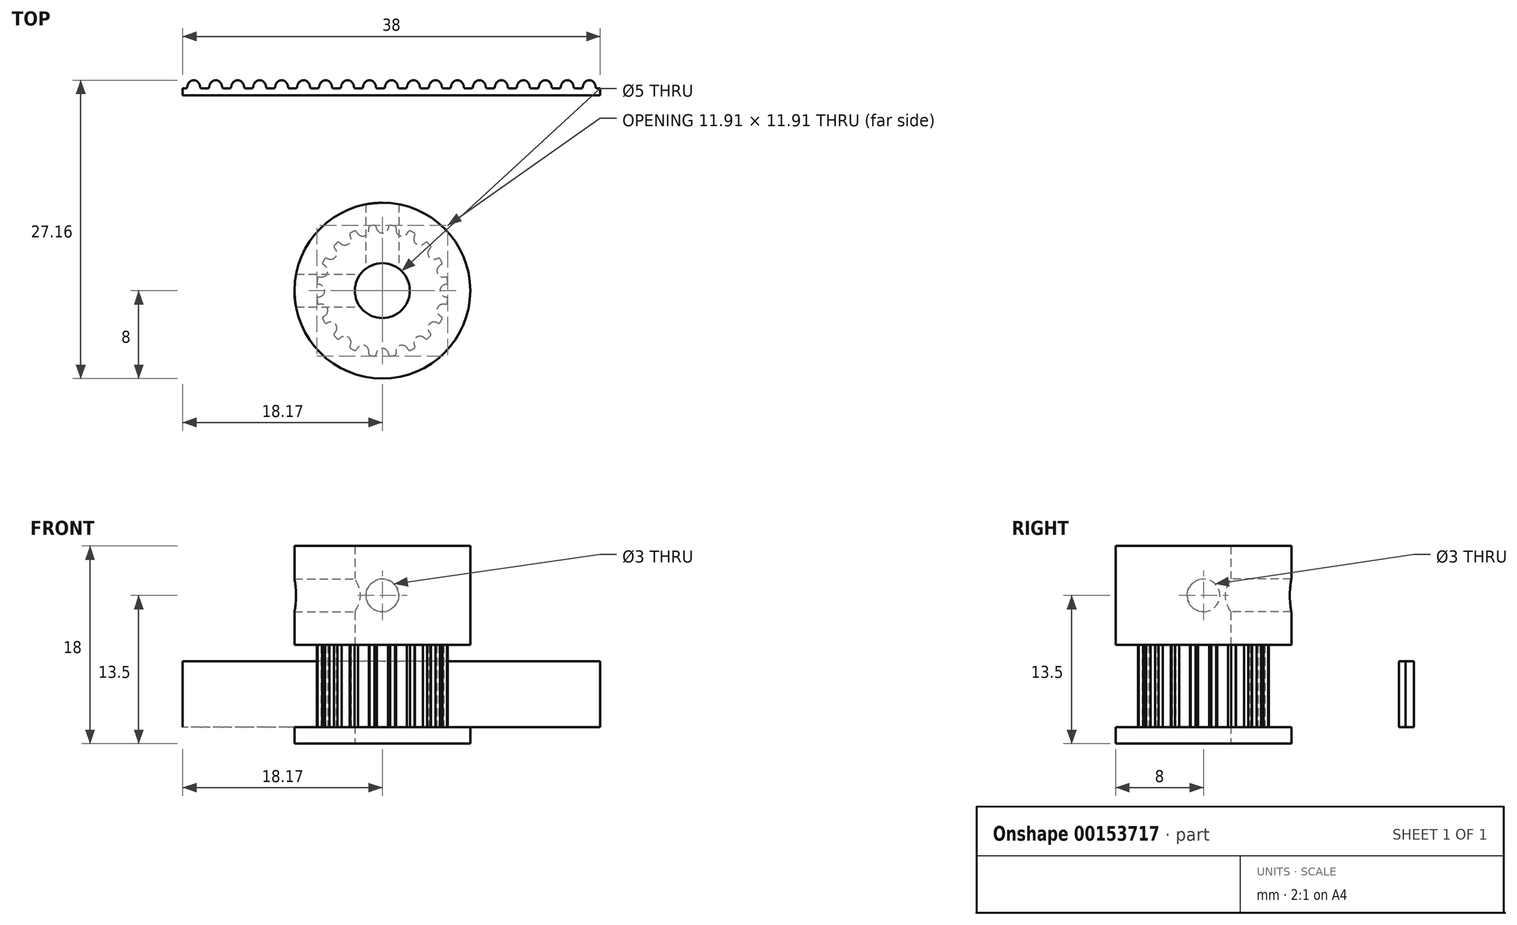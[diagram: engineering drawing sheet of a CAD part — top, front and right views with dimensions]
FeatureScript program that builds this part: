
annotation { "Feature Type Name" : "Feature", "Feature Type Description" : "" }
export const myFeature = defineFeature(function(context is Context, id is Id, definition is map)
    precondition{}
    {
        {
            var Q0;
            Q0=qCreatedBy(makeId("Top.planeOp"),FACE);
            var sketch = newSketch(context, id + "F0", { "sketchPlane" : qUnion([Q0])});
            skLineSegment(sketch, "E0", {"start": v(-19.17, 17.78) * mm, "end": v(-18.17, 17.78) * mm});
            skLineSegment(sketch, "E1", {"start": v(-18.17, 17.78) * mm, "end": v(-18.17, 18.4) * mm});
            skArc(sketch, "E2", {"start": v(-18.67, 18.85) * mm, "mid": v(-18.88, 19.07) * mm, "end": v(-19.17, 19.16) * mm});
            skArc(sketch, "E3", {"start": v(-18.58, 18.54) * mm, "mid": v(-18.61, 18.7) * mm, "end": v(-18.67, 18.85) * mm});
            skArc(sketch, "E4", {"start": v(-18.58, 18.54) * mm, "mid": v(-18.53, 18.44) * mm, "end": v(-18.43, 18.4) * mm});
            skLineSegment(sketch, "E5", {"start": v(-18.43, 18.4) * mm, "end": v(-18.17, 18.4) * mm});
            skArc(sketch, "E6.0.MirrorCS", {"start": v(-19.67, 18.85) * mm, "mid": v(-19.47, 19.07) * mm, "end": v(-19.17, 19.16) * mm});
            skArc(sketch, "E7.0.MirrorCS", {"start": v(-19.76, 18.54) * mm, "mid": v(-19.73, 18.7) * mm, "end": v(-19.67, 18.85) * mm});
            skArc(sketch, "E8.0.MirrorCS", {"start": v(-19.76, 18.54) * mm, "mid": v(-19.81, 18.44) * mm, "end": v(-19.91, 18.4) * mm});
            skLineSegment(sketch, "E9.0.MirrorCS", {"start": v(-19.91, 18.4) * mm, "end": v(-20.17, 18.4) * mm});
            skLineSegment(sketch, "E10.0.MirrorCS", {"start": v(-20.17, 17.78) * mm, "end": v(-20.17, 18.4) * mm});
            skLineSegment(sketch, "E11.0.MirrorCS", {"start": v(-19.17, 17.78) * mm, "end": v(-20.17, 17.78) * mm});
            skLineSegment(sketch, "E12.direction1", {"start": v(-20.17, 17.78) * mm, "end": v(-18.17, 17.78) * mm, "construction": true});
            skLineSegment(sketch, "E13", {"start": v(-20.17, 18.15) * mm, "end": v(-18.17, 18.15) * mm, "construction": true});
            skPoint(sketch, "E14", {"position": v(0, -5.25) * mm});
            skArc(sketch, "E15", {"start": v(0.51, -5.6) * mm, "mid": v(0, -5.25) * mm, "end": v(-0.51, -5.6) * mm});
            skArc(sketch, "E16", {"start": v(-0.51, -5.6) * mm, "mid": v(-0.56, -5.71) * mm, "end": v(-0.59, -5.83) * mm});
            skArc(sketch, "E17", {"start": v(0.59, -5.83) * mm, "mid": v(0.56, -5.71) * mm, "end": v(0.51, -5.6) * mm});
            skArc(sketch, "E18", {"start": v(0.72, -5.96) * mm, "mid": v(0.94, -5.93) * mm, "end": v(1.16, -5.89) * mm});
            skArc(sketch, "E19", {"start": v(0.59, -5.83) * mm, "mid": v(0.66, -5.94) * mm, "end": v(0.8, -5.95) * mm});
            skArc(sketch, "E20", {"start": v(-0.59, -5.83) * mm, "mid": v(-0.66, -5.94) * mm, "end": v(-0.8, -5.95) * mm});
            skArc(sketch, "E21.1.0", {"start": v(2.22, -5.16) * mm, "mid": v(1.62, -5) * mm, "end": v(1.24, -5.48) * mm});
            skPoint(sketch, "E21.1.1", {"position": v(1.62, -5) * mm});
            skArc(sketch, "E21.1.2", {"start": v(1.24, -5.48) * mm, "mid": v(1.23, -5.6) * mm, "end": v(1.24, -5.73) * mm});
            skArc(sketch, "E21.1.3", {"start": v(2.36, -5.37) * mm, "mid": v(2.47, -5.44) * mm, "end": v(2.6, -5.41) * mm});
            skArc(sketch, "E21.1.4", {"start": v(1.24, -5.73) * mm, "mid": v(1.2, -5.85) * mm, "end": v(1.08, -5.9) * mm});
            skArc(sketch, "E21.1.5", {"start": v(2.36, -5.37) * mm, "mid": v(2.3, -5.26) * mm, "end": v(2.22, -5.16) * mm});
            skArc(sketch, "E22.3.2.0", {"start": v(3.7, -4.22) * mm, "mid": v(3.09, -4.25) * mm, "end": v(2.87, -4.83) * mm});
            skPoint(sketch, "E22.4.2.0", {"position": v(3.09, -4.25) * mm});
            skArc(sketch, "E22.5.2.0", {"start": v(2.87, -4.83) * mm, "mid": v(2.9, -4.95) * mm, "end": v(2.95, -5.07) * mm});
            skArc(sketch, "E22.9.2.0", {"start": v(3.9, -4.37) * mm, "mid": v(4.03, -4.41) * mm, "end": v(4.14, -4.35) * mm});
            skArc(sketch, "E22.13.2.0", {"start": v(2.95, -5.07) * mm, "mid": v(2.95, -5.2) * mm, "end": v(2.85, -5.28) * mm});
            skArc(sketch, "E22.17.2.0", {"start": v(3.9, -4.37) * mm, "mid": v(3.81, -4.3) * mm, "end": v(3.7, -4.22) * mm});
            skArc(sketch, "E22.3.3.0", {"start": v(4.83, -2.87) * mm, "mid": v(4.25, -3.09) * mm, "end": v(4.22, -3.7) * mm});
            skPoint(sketch, "E22.4.3.0", {"position": v(4.25, -3.09) * mm});
            skArc(sketch, "E22.5.3.0", {"start": v(4.22, -3.7) * mm, "mid": v(4.3, -3.81) * mm, "end": v(4.37, -3.9) * mm});
            skArc(sketch, "E22.9.3.0", {"start": v(5.07, -2.95) * mm, "mid": v(5.2, -2.95) * mm, "end": v(5.28, -2.85) * mm});
            skArc(sketch, "E22.13.3.0", {"start": v(4.37, -3.9) * mm, "mid": v(4.41, -4.03) * mm, "end": v(4.35, -4.14) * mm});
            skArc(sketch, "E22.17.3.0", {"start": v(5.07, -2.95) * mm, "mid": v(4.95, -2.9) * mm, "end": v(4.83, -2.87) * mm});
            skArc(sketch, "E22.3.4.0", {"start": v(5.48, -1.24) * mm, "mid": v(5, -1.62) * mm, "end": v(5.16, -2.22) * mm});
            skPoint(sketch, "E22.4.4.0", {"position": v(5, -1.62) * mm});
            skArc(sketch, "E22.5.4.0", {"start": v(5.16, -2.22) * mm, "mid": v(5.26, -2.3) * mm, "end": v(5.37, -2.36) * mm});
            skArc(sketch, "E22.9.4.0", {"start": v(5.73, -1.24) * mm, "mid": v(5.85, -1.2) * mm, "end": v(5.9, -1.08) * mm});
            skArc(sketch, "E22.13.4.0", {"start": v(5.37, -2.36) * mm, "mid": v(5.44, -2.47) * mm, "end": v(5.41, -2.6) * mm});
            skArc(sketch, "E22.17.4.0", {"start": v(5.73, -1.24) * mm, "mid": v(5.6, -1.23) * mm, "end": v(5.48, -1.24) * mm});
            skArc(sketch, "E22.3.5.0", {"start": v(5.6, 0.51) * mm, "mid": v(5.25, 0) * mm, "end": v(5.6, -0.51) * mm});
            skPoint(sketch, "E22.4.5.0", {"position": v(5.25, 0) * mm});
            skArc(sketch, "E22.5.5.0", {"start": v(5.6, -0.51) * mm, "mid": v(5.71, -0.56) * mm, "end": v(5.83, -0.59) * mm});
            skArc(sketch, "E22.9.5.0", {"start": v(5.83, 0.59) * mm, "mid": v(5.94, 0.66) * mm, "end": v(5.95, 0.8) * mm});
            skArc(sketch, "E22.13.5.0", {"start": v(5.83, -0.59) * mm, "mid": v(5.94, -0.66) * mm, "end": v(5.95, -0.8) * mm});
            skArc(sketch, "E22.17.5.0", {"start": v(5.83, 0.59) * mm, "mid": v(5.71, 0.56) * mm, "end": v(5.6, 0.51) * mm});
            skArc(sketch, "E22.3.6.0", {"start": v(5.16, 2.22) * mm, "mid": v(5, 1.62) * mm, "end": v(5.48, 1.24) * mm});
            skPoint(sketch, "E22.4.6.0", {"position": v(5, 1.62) * mm});
            skArc(sketch, "E22.5.6.0", {"start": v(5.48, 1.24) * mm, "mid": v(5.6, 1.23) * mm, "end": v(5.73, 1.24) * mm});
            skArc(sketch, "E22.9.6.0", {"start": v(5.37, 2.36) * mm, "mid": v(5.44, 2.47) * mm, "end": v(5.41, 2.6) * mm});
            skArc(sketch, "E22.13.6.0", {"start": v(5.73, 1.24) * mm, "mid": v(5.85, 1.2) * mm, "end": v(5.9, 1.08) * mm});
            skArc(sketch, "E22.17.6.0", {"start": v(5.37, 2.36) * mm, "mid": v(5.26, 2.3) * mm, "end": v(5.16, 2.22) * mm});
            skArc(sketch, "E22.3.7.0", {"start": v(4.22, 3.7) * mm, "mid": v(4.25, 3.09) * mm, "end": v(4.83, 2.87) * mm});
            skPoint(sketch, "E22.4.7.0", {"position": v(4.25, 3.09) * mm});
            skArc(sketch, "E22.5.7.0", {"start": v(4.83, 2.87) * mm, "mid": v(4.95, 2.9) * mm, "end": v(5.07, 2.95) * mm});
            skArc(sketch, "E22.9.7.0", {"start": v(4.37, 3.9) * mm, "mid": v(4.41, 4.03) * mm, "end": v(4.35, 4.14) * mm});
            skArc(sketch, "E22.13.7.0", {"start": v(5.07, 2.95) * mm, "mid": v(5.2, 2.95) * mm, "end": v(5.28, 2.85) * mm});
            skArc(sketch, "E22.17.7.0", {"start": v(4.37, 3.9) * mm, "mid": v(4.3, 3.81) * mm, "end": v(4.22, 3.7) * mm});
            skArc(sketch, "E22.3.8.0", {"start": v(2.87, 4.83) * mm, "mid": v(3.09, 4.25) * mm, "end": v(3.7, 4.22) * mm});
            skPoint(sketch, "E22.4.8.0", {"position": v(3.09, 4.25) * mm});
            skArc(sketch, "E22.5.8.0", {"start": v(3.7, 4.22) * mm, "mid": v(3.81, 4.3) * mm, "end": v(3.9, 4.37) * mm});
            skArc(sketch, "E22.9.8.0", {"start": v(2.95, 5.07) * mm, "mid": v(2.95, 5.2) * mm, "end": v(2.85, 5.28) * mm});
            skArc(sketch, "E22.13.8.0", {"start": v(3.9, 4.37) * mm, "mid": v(4.03, 4.41) * mm, "end": v(4.14, 4.35) * mm});
            skArc(sketch, "E22.17.8.0", {"start": v(2.95, 5.07) * mm, "mid": v(2.9, 4.95) * mm, "end": v(2.87, 4.83) * mm});
            skArc(sketch, "E22.3.9.0", {"start": v(1.24, 5.48) * mm, "mid": v(1.62, 5) * mm, "end": v(2.22, 5.16) * mm});
            skPoint(sketch, "E22.4.9.0", {"position": v(1.62, 5) * mm});
            skArc(sketch, "E22.5.9.0", {"start": v(2.22, 5.16) * mm, "mid": v(2.3, 5.26) * mm, "end": v(2.36, 5.37) * mm});
            skArc(sketch, "E22.9.9.0", {"start": v(1.24, 5.73) * mm, "mid": v(1.2, 5.85) * mm, "end": v(1.08, 5.9) * mm});
            skArc(sketch, "E22.13.9.0", {"start": v(2.36, 5.37) * mm, "mid": v(2.47, 5.44) * mm, "end": v(2.6, 5.41) * mm});
            skArc(sketch, "E22.17.9.0", {"start": v(1.24, 5.73) * mm, "mid": v(1.23, 5.6) * mm, "end": v(1.24, 5.48) * mm});
            skArc(sketch, "E22.3.10.0", {"start": v(-0.51, 5.6) * mm, "mid": v(0, 5.25) * mm, "end": v(0.51, 5.6) * mm});
            skPoint(sketch, "E22.4.10.0", {"position": v(0, 5.25) * mm});
            skArc(sketch, "E22.5.10.0", {"start": v(0.51, 5.6) * mm, "mid": v(0.56, 5.71) * mm, "end": v(0.59, 5.83) * mm});
            skArc(sketch, "E22.9.10.0", {"start": v(-0.59, 5.83) * mm, "mid": v(-0.66, 5.94) * mm, "end": v(-0.8, 5.95) * mm});
            skArc(sketch, "E22.13.10.0", {"start": v(0.59, 5.83) * mm, "mid": v(0.66, 5.94) * mm, "end": v(0.8, 5.95) * mm});
            skArc(sketch, "E22.17.10.0", {"start": v(-0.59, 5.83) * mm, "mid": v(-0.56, 5.71) * mm, "end": v(-0.51, 5.6) * mm});
            skArc(sketch, "E22.3.11.0", {"start": v(-2.22, 5.16) * mm, "mid": v(-1.62, 5) * mm, "end": v(-1.24, 5.48) * mm});
            skPoint(sketch, "E22.4.11.0", {"position": v(-1.62, 5) * mm});
            skArc(sketch, "E22.5.11.0", {"start": v(-1.24, 5.48) * mm, "mid": v(-1.23, 5.6) * mm, "end": v(-1.24, 5.73) * mm});
            skArc(sketch, "E22.9.11.0", {"start": v(-2.36, 5.37) * mm, "mid": v(-2.47, 5.44) * mm, "end": v(-2.6, 5.41) * mm});
            skArc(sketch, "E22.13.11.0", {"start": v(-1.24, 5.73) * mm, "mid": v(-1.2, 5.85) * mm, "end": v(-1.08, 5.9) * mm});
            skArc(sketch, "E22.17.11.0", {"start": v(-2.36, 5.37) * mm, "mid": v(-2.3, 5.26) * mm, "end": v(-2.22, 5.16) * mm});
            skArc(sketch, "E22.3.12.0", {"start": v(-3.7, 4.22) * mm, "mid": v(-3.09, 4.25) * mm, "end": v(-2.87, 4.83) * mm});
            skPoint(sketch, "E22.4.12.0", {"position": v(-3.09, 4.25) * mm});
            skArc(sketch, "E22.5.12.0", {"start": v(-2.87, 4.83) * mm, "mid": v(-2.9, 4.95) * mm, "end": v(-2.95, 5.07) * mm});
            skArc(sketch, "E22.9.12.0", {"start": v(-3.9, 4.37) * mm, "mid": v(-4.03, 4.41) * mm, "end": v(-4.14, 4.35) * mm});
            skArc(sketch, "E22.13.12.0", {"start": v(-2.95, 5.07) * mm, "mid": v(-2.95, 5.2) * mm, "end": v(-2.85, 5.28) * mm});
            skArc(sketch, "E22.17.12.0", {"start": v(-3.9, 4.37) * mm, "mid": v(-3.81, 4.3) * mm, "end": v(-3.7, 4.22) * mm});
            skArc(sketch, "E22.3.13.0", {"start": v(-4.83, 2.87) * mm, "mid": v(-4.25, 3.09) * mm, "end": v(-4.22, 3.7) * mm});
            skPoint(sketch, "E22.4.13.0", {"position": v(-4.25, 3.09) * mm});
            skArc(sketch, "E22.5.13.0", {"start": v(-4.22, 3.7) * mm, "mid": v(-4.3, 3.81) * mm, "end": v(-4.37, 3.9) * mm});
            skArc(sketch, "E22.9.13.0", {"start": v(-5.07, 2.95) * mm, "mid": v(-5.2, 2.95) * mm, "end": v(-5.28, 2.85) * mm});
            skArc(sketch, "E22.13.13.0", {"start": v(-4.37, 3.9) * mm, "mid": v(-4.41, 4.03) * mm, "end": v(-4.35, 4.14) * mm});
            skArc(sketch, "E22.17.13.0", {"start": v(-5.07, 2.95) * mm, "mid": v(-4.95, 2.9) * mm, "end": v(-4.83, 2.87) * mm});
            skArc(sketch, "E22.3.14.0", {"start": v(-5.48, 1.24) * mm, "mid": v(-5, 1.62) * mm, "end": v(-5.16, 2.22) * mm});
            skPoint(sketch, "E22.4.14.0", {"position": v(-5, 1.62) * mm});
            skArc(sketch, "E22.5.14.0", {"start": v(-5.16, 2.22) * mm, "mid": v(-5.26, 2.3) * mm, "end": v(-5.37, 2.36) * mm});
            skArc(sketch, "E22.9.14.0", {"start": v(-5.73, 1.24) * mm, "mid": v(-5.85, 1.2) * mm, "end": v(-5.9, 1.08) * mm});
            skArc(sketch, "E22.13.14.0", {"start": v(-5.37, 2.36) * mm, "mid": v(-5.44, 2.47) * mm, "end": v(-5.41, 2.6) * mm});
            skArc(sketch, "E22.17.14.0", {"start": v(-5.73, 1.24) * mm, "mid": v(-5.6, 1.23) * mm, "end": v(-5.48, 1.24) * mm});
            skArc(sketch, "E22.3.15.0", {"start": v(-5.6, -0.51) * mm, "mid": v(-5.25, 0) * mm, "end": v(-5.6, 0.51) * mm});
            skPoint(sketch, "E22.4.15.0", {"position": v(-5.25, 0) * mm});
            skArc(sketch, "E22.5.15.0", {"start": v(-5.6, 0.51) * mm, "mid": v(-5.71, 0.56) * mm, "end": v(-5.83, 0.59) * mm});
            skArc(sketch, "E22.9.15.0", {"start": v(-5.83, -0.59) * mm, "mid": v(-5.94, -0.66) * mm, "end": v(-5.95, -0.8) * mm});
            skArc(sketch, "E22.13.15.0", {"start": v(-5.83, 0.59) * mm, "mid": v(-5.94, 0.66) * mm, "end": v(-5.95, 0.8) * mm});
            skArc(sketch, "E22.17.15.0", {"start": v(-5.83, -0.59) * mm, "mid": v(-5.71, -0.56) * mm, "end": v(-5.6, -0.51) * mm});
            skArc(sketch, "E22.3.16.0", {"start": v(-5.16, -2.22) * mm, "mid": v(-5, -1.62) * mm, "end": v(-5.48, -1.24) * mm});
            skPoint(sketch, "E22.4.16.0", {"position": v(-5, -1.62) * mm});
            skArc(sketch, "E22.5.16.0", {"start": v(-5.48, -1.24) * mm, "mid": v(-5.6, -1.23) * mm, "end": v(-5.73, -1.24) * mm});
            skArc(sketch, "E22.9.16.0", {"start": v(-5.37, -2.36) * mm, "mid": v(-5.44, -2.47) * mm, "end": v(-5.41, -2.6) * mm});
            skArc(sketch, "E22.13.16.0", {"start": v(-5.73, -1.24) * mm, "mid": v(-5.85, -1.2) * mm, "end": v(-5.9, -1.08) * mm});
            skArc(sketch, "E22.17.16.0", {"start": v(-5.37, -2.36) * mm, "mid": v(-5.26, -2.3) * mm, "end": v(-5.16, -2.22) * mm});
            skArc(sketch, "E22.3.17.0", {"start": v(-4.22, -3.7) * mm, "mid": v(-4.25, -3.09) * mm, "end": v(-4.83, -2.87) * mm});
            skPoint(sketch, "E22.4.17.0", {"position": v(-4.25, -3.09) * mm});
            skArc(sketch, "E22.5.17.0", {"start": v(-4.83, -2.87) * mm, "mid": v(-4.95, -2.9) * mm, "end": v(-5.07, -2.95) * mm});
            skArc(sketch, "E22.9.17.0", {"start": v(-4.37, -3.9) * mm, "mid": v(-4.41, -4.03) * mm, "end": v(-4.35, -4.14) * mm});
            skArc(sketch, "E22.13.17.0", {"start": v(-5.07, -2.95) * mm, "mid": v(-5.2, -2.95) * mm, "end": v(-5.28, -2.85) * mm});
            skArc(sketch, "E22.17.17.0", {"start": v(-4.37, -3.9) * mm, "mid": v(-4.3, -3.81) * mm, "end": v(-4.22, -3.7) * mm});
            skArc(sketch, "E22.3.18.0", {"start": v(-2.87, -4.83) * mm, "mid": v(-3.09, -4.25) * mm, "end": v(-3.7, -4.22) * mm});
            skPoint(sketch, "E22.4.18.0", {"position": v(-3.09, -4.25) * mm});
            skArc(sketch, "E22.5.18.0", {"start": v(-3.7, -4.22) * mm, "mid": v(-3.81, -4.3) * mm, "end": v(-3.9, -4.37) * mm});
            skArc(sketch, "E22.9.18.0", {"start": v(-2.95, -5.07) * mm, "mid": v(-2.95, -5.2) * mm, "end": v(-2.85, -5.28) * mm});
            skArc(sketch, "E22.13.18.0", {"start": v(-3.9, -4.37) * mm, "mid": v(-4.03, -4.41) * mm, "end": v(-4.14, -4.35) * mm});
            skArc(sketch, "E22.17.18.0", {"start": v(-2.95, -5.07) * mm, "mid": v(-2.9, -4.95) * mm, "end": v(-2.87, -4.83) * mm});
            skArc(sketch, "E22.3.19.0", {"start": v(-1.24, -5.48) * mm, "mid": v(-1.62, -5) * mm, "end": v(-2.22, -5.16) * mm});
            skPoint(sketch, "E22.4.19.0", {"position": v(-1.62, -5) * mm});
            skArc(sketch, "E22.5.19.0", {"start": v(-2.22, -5.16) * mm, "mid": v(-2.3, -5.26) * mm, "end": v(-2.36, -5.37) * mm});
            skArc(sketch, "E22.9.19.0", {"start": v(-1.24, -5.73) * mm, "mid": v(-1.2, -5.85) * mm, "end": v(-1.08, -5.9) * mm});
            skArc(sketch, "E22.13.19.0", {"start": v(-2.36, -5.37) * mm, "mid": v(-2.47, -5.44) * mm, "end": v(-2.6, -5.41) * mm});
            skArc(sketch, "E22.17.19.0", {"start": v(-1.24, -5.73) * mm, "mid": v(-1.23, -5.6) * mm, "end": v(-1.24, -5.48) * mm});
            skArc(sketch, "E23.trimOffspring", {"start": v(2.52, -5.44) * mm, "mid": v(2.72, -5.35) * mm, "end": v(2.92, -5.24) * mm});
            skArc(sketch, "E24.trimOffspring", {"start": v(4.08, -4.4) * mm, "mid": v(4.24, -4.24) * mm, "end": v(4.4, -4.08) * mm});
            skArc(sketch, "E25.trimOffspring", {"start": v(5.24, -2.92) * mm, "mid": v(5.33, -2.76) * mm, "end": v(5.41, -2.6) * mm});
            skArc(sketch, "E26.trimOffspring", {"start": v(5.89, -1.16) * mm, "mid": v(5.93, -0.94) * mm, "end": v(5.96, -0.72) * mm});
            skArc(sketch, "E27.trimOffspring", {"start": v(5.44, 2.52) * mm, "mid": v(5.35, 2.72) * mm, "end": v(5.24, 2.92) * mm});
            skArc(sketch, "E28.trimOffspring", {"start": v(4.4, 4.08) * mm, "mid": v(4.24, 4.24) * mm, "end": v(4.08, 4.4) * mm});
            skArc(sketch, "E29.trimOffspring", {"start": v(5.96, 0.72) * mm, "mid": v(5.93, 0.94) * mm, "end": v(5.89, 1.16) * mm});
            skArc(sketch, "E30.trimOffspring", {"start": v(2.92, 5.24) * mm, "mid": v(2.72, 5.35) * mm, "end": v(2.52, 5.44) * mm});
            skArc(sketch, "E31.trimOffspring", {"start": v(1.16, 5.89) * mm, "mid": v(0.94, 5.93) * mm, "end": v(0.72, 5.96) * mm});
            skArc(sketch, "E32.trimOffspring", {"start": v(-0.72, 5.96) * mm, "mid": v(-0.94, 5.93) * mm, "end": v(-1.16, 5.89) * mm});
            skArc(sketch, "E33.trimOffspring", {"start": v(-2.52, 5.44) * mm, "mid": v(-2.72, 5.35) * mm, "end": v(-2.92, 5.24) * mm});
            skArc(sketch, "E34.trimOffspring", {"start": v(-4.08, 4.4) * mm, "mid": v(-4.24, 4.24) * mm, "end": v(-4.4, 4.08) * mm});
            skArc(sketch, "E35.trimOffspring", {"start": v(-5.24, 2.92) * mm, "mid": v(-5.35, 2.72) * mm, "end": v(-5.44, 2.52) * mm});
            skArc(sketch, "E36.trimOffspring", {"start": v(-5.89, 1.16) * mm, "mid": v(-5.93, 0.94) * mm, "end": v(-5.96, 0.72) * mm});
            skArc(sketch, "E37.trimOffspring", {"start": v(-5.96, -0.72) * mm, "mid": v(-5.93, -0.94) * mm, "end": v(-5.89, -1.16) * mm});
            skArc(sketch, "E38.trimOffspring", {"start": v(-5.44, -2.52) * mm, "mid": v(-5.35, -2.72) * mm, "end": v(-5.24, -2.92) * mm});
            skArc(sketch, "E39.trimOffspring", {"start": v(-4.4, -4.08) * mm, "mid": v(-4.24, -4.24) * mm, "end": v(-4.08, -4.4) * mm});
            skArc(sketch, "E40.trimOffspring", {"start": v(-2.92, -5.24) * mm, "mid": v(-2.72, -5.35) * mm, "end": v(-2.52, -5.44) * mm});
            skArc(sketch, "E41.trimOffspring", {"start": v(-1.16, -5.89) * mm, "mid": v(-0.94, -5.93) * mm, "end": v(-0.72, -5.96) * mm});
            skArc(sketch, "E42.1.0.0", {"start": v(-16.67, 18.85) * mm, "mid": v(-16.88, 19.07) * mm, "end": v(-17.17, 19.16) * mm});
            skArc(sketch, "E42.1.0.1", {"start": v(-16.58, 18.54) * mm, "mid": v(-16.61, 18.7) * mm, "end": v(-16.67, 18.85) * mm});
            skArc(sketch, "E42.1.0.2", {"start": v(-16.58, 18.54) * mm, "mid": v(-16.53, 18.44) * mm, "end": v(-16.43, 18.4) * mm});
            skLineSegment(sketch, "E42.1.0.3", {"start": v(-16.43, 18.4) * mm, "end": v(-16.17, 18.4) * mm});
            skArc(sketch, "E42.1.0.4", {"start": v(-17.67, 18.85) * mm, "mid": v(-17.47, 19.07) * mm, "end": v(-17.17, 19.16) * mm});
            skArc(sketch, "E42.1.0.5", {"start": v(-17.76, 18.54) * mm, "mid": v(-17.73, 18.7) * mm, "end": v(-17.67, 18.85) * mm});
            skArc(sketch, "E42.1.0.6", {"start": v(-17.76, 18.54) * mm, "mid": v(-17.81, 18.44) * mm, "end": v(-17.91, 18.4) * mm});
            skLineSegment(sketch, "E42.1.0.7", {"start": v(-17.91, 18.4) * mm, "end": v(-18.17, 18.4) * mm});
            skArc(sketch, "E42.2.0.0", {"start": v(-14.67, 18.85) * mm, "mid": v(-14.88, 19.07) * mm, "end": v(-15.17, 19.16) * mm});
            skArc(sketch, "E42.2.0.1", {"start": v(-14.58, 18.54) * mm, "mid": v(-14.61, 18.7) * mm, "end": v(-14.67, 18.85) * mm});
            skArc(sketch, "E42.2.0.2", {"start": v(-14.58, 18.54) * mm, "mid": v(-14.53, 18.44) * mm, "end": v(-14.43, 18.4) * mm});
            skLineSegment(sketch, "E42.2.0.3", {"start": v(-14.43, 18.4) * mm, "end": v(-14.17, 18.4) * mm});
            skArc(sketch, "E42.2.0.4", {"start": v(-15.67, 18.85) * mm, "mid": v(-15.47, 19.07) * mm, "end": v(-15.17, 19.16) * mm});
            skArc(sketch, "E42.2.0.5", {"start": v(-15.76, 18.54) * mm, "mid": v(-15.73, 18.7) * mm, "end": v(-15.67, 18.85) * mm});
            skArc(sketch, "E42.2.0.6", {"start": v(-15.76, 18.54) * mm, "mid": v(-15.81, 18.44) * mm, "end": v(-15.91, 18.4) * mm});
            skLineSegment(sketch, "E42.2.0.7", {"start": v(-15.91, 18.4) * mm, "end": v(-16.17, 18.4) * mm});
            skArc(sketch, "E42.3.0.0", {"start": v(-12.67, 18.85) * mm, "mid": v(-12.88, 19.07) * mm, "end": v(-13.17, 19.16) * mm});
            skArc(sketch, "E42.3.0.1", {"start": v(-12.58, 18.54) * mm, "mid": v(-12.61, 18.7) * mm, "end": v(-12.67, 18.85) * mm});
            skArc(sketch, "E42.3.0.2", {"start": v(-12.58, 18.54) * mm, "mid": v(-12.53, 18.44) * mm, "end": v(-12.43, 18.4) * mm});
            skLineSegment(sketch, "E42.3.0.3", {"start": v(-12.43, 18.4) * mm, "end": v(-12.17, 18.4) * mm});
            skArc(sketch, "E42.3.0.4", {"start": v(-13.67, 18.85) * mm, "mid": v(-13.47, 19.07) * mm, "end": v(-13.17, 19.16) * mm});
            skArc(sketch, "E42.3.0.5", {"start": v(-13.76, 18.54) * mm, "mid": v(-13.73, 18.7) * mm, "end": v(-13.67, 18.85) * mm});
            skArc(sketch, "E42.3.0.6", {"start": v(-13.76, 18.54) * mm, "mid": v(-13.81, 18.44) * mm, "end": v(-13.91, 18.4) * mm});
            skLineSegment(sketch, "E42.3.0.7", {"start": v(-13.91, 18.4) * mm, "end": v(-14.17, 18.4) * mm});
            skArc(sketch, "E42.4.0.0", {"start": v(-10.67, 18.85) * mm, "mid": v(-10.88, 19.07) * mm, "end": v(-11.17, 19.16) * mm});
            skArc(sketch, "E42.4.0.1", {"start": v(-10.58, 18.54) * mm, "mid": v(-10.61, 18.7) * mm, "end": v(-10.67, 18.85) * mm});
            skArc(sketch, "E42.4.0.2", {"start": v(-10.58, 18.54) * mm, "mid": v(-10.53, 18.44) * mm, "end": v(-10.43, 18.4) * mm});
            skLineSegment(sketch, "E42.4.0.3", {"start": v(-10.43, 18.4) * mm, "end": v(-10.17, 18.4) * mm});
            skArc(sketch, "E42.4.0.4", {"start": v(-11.67, 18.85) * mm, "mid": v(-11.47, 19.07) * mm, "end": v(-11.17, 19.16) * mm});
            skArc(sketch, "E42.4.0.5", {"start": v(-11.76, 18.54) * mm, "mid": v(-11.73, 18.7) * mm, "end": v(-11.67, 18.85) * mm});
            skArc(sketch, "E42.4.0.6", {"start": v(-11.76, 18.54) * mm, "mid": v(-11.81, 18.44) * mm, "end": v(-11.91, 18.4) * mm});
            skLineSegment(sketch, "E42.4.0.7", {"start": v(-11.91, 18.4) * mm, "end": v(-12.17, 18.4) * mm});
            skArc(sketch, "E42.5.0.0", {"start": v(-8.67, 18.85) * mm, "mid": v(-8.88, 19.07) * mm, "end": v(-9.17, 19.16) * mm});
            skArc(sketch, "E42.5.0.1", {"start": v(-8.58, 18.54) * mm, "mid": v(-8.61, 18.7) * mm, "end": v(-8.67, 18.85) * mm});
            skArc(sketch, "E42.5.0.2", {"start": v(-8.58, 18.54) * mm, "mid": v(-8.53, 18.44) * mm, "end": v(-8.43, 18.4) * mm});
            skLineSegment(sketch, "E42.5.0.3", {"start": v(-8.43, 18.4) * mm, "end": v(-8.17, 18.4) * mm});
            skArc(sketch, "E42.5.0.4", {"start": v(-9.67, 18.85) * mm, "mid": v(-9.47, 19.07) * mm, "end": v(-9.17, 19.16) * mm});
            skArc(sketch, "E42.5.0.5", {"start": v(-9.76, 18.54) * mm, "mid": v(-9.73, 18.7) * mm, "end": v(-9.67, 18.85) * mm});
            skArc(sketch, "E42.5.0.6", {"start": v(-9.76, 18.54) * mm, "mid": v(-9.81, 18.44) * mm, "end": v(-9.91, 18.4) * mm});
            skLineSegment(sketch, "E42.5.0.7", {"start": v(-9.91, 18.4) * mm, "end": v(-10.17, 18.4) * mm});
            skArc(sketch, "E42.6.0.0", {"start": v(-6.67, 18.85) * mm, "mid": v(-6.88, 19.07) * mm, "end": v(-7.17, 19.16) * mm});
            skArc(sketch, "E42.6.0.1", {"start": v(-6.58, 18.54) * mm, "mid": v(-6.61, 18.7) * mm, "end": v(-6.67, 18.85) * mm});
            skArc(sketch, "E42.6.0.2", {"start": v(-6.58, 18.54) * mm, "mid": v(-6.53, 18.44) * mm, "end": v(-6.43, 18.4) * mm});
            skLineSegment(sketch, "E42.6.0.3", {"start": v(-6.43, 18.4) * mm, "end": v(-6.17, 18.4) * mm});
            skArc(sketch, "E42.6.0.4", {"start": v(-7.67, 18.85) * mm, "mid": v(-7.47, 19.07) * mm, "end": v(-7.17, 19.16) * mm});
            skArc(sketch, "E42.6.0.5", {"start": v(-7.76, 18.54) * mm, "mid": v(-7.73, 18.7) * mm, "end": v(-7.67, 18.85) * mm});
            skArc(sketch, "E42.6.0.6", {"start": v(-7.76, 18.54) * mm, "mid": v(-7.81, 18.44) * mm, "end": v(-7.91, 18.4) * mm});
            skLineSegment(sketch, "E42.6.0.7", {"start": v(-7.91, 18.4) * mm, "end": v(-8.17, 18.4) * mm});
            skArc(sketch, "E42.7.0.0", {"start": v(-4.67, 18.85) * mm, "mid": v(-4.88, 19.07) * mm, "end": v(-5.17, 19.16) * mm});
            skArc(sketch, "E42.7.0.1", {"start": v(-4.58, 18.54) * mm, "mid": v(-4.61, 18.7) * mm, "end": v(-4.67, 18.85) * mm});
            skArc(sketch, "E42.7.0.2", {"start": v(-4.58, 18.54) * mm, "mid": v(-4.53, 18.44) * mm, "end": v(-4.43, 18.4) * mm});
            skLineSegment(sketch, "E42.7.0.3", {"start": v(-4.43, 18.4) * mm, "end": v(-4.17, 18.4) * mm});
            skArc(sketch, "E42.7.0.4", {"start": v(-5.67, 18.85) * mm, "mid": v(-5.47, 19.07) * mm, "end": v(-5.17, 19.16) * mm});
            skArc(sketch, "E42.7.0.5", {"start": v(-5.76, 18.54) * mm, "mid": v(-5.73, 18.7) * mm, "end": v(-5.67, 18.85) * mm});
            skArc(sketch, "E42.7.0.6", {"start": v(-5.76, 18.54) * mm, "mid": v(-5.81, 18.44) * mm, "end": v(-5.91, 18.4) * mm});
            skLineSegment(sketch, "E42.7.0.7", {"start": v(-5.91, 18.4) * mm, "end": v(-6.17, 18.4) * mm});
            skArc(sketch, "E42.8.0.0", {"start": v(-2.67, 18.85) * mm, "mid": v(-2.88, 19.07) * mm, "end": v(-3.17, 19.16) * mm});
            skArc(sketch, "E42.8.0.1", {"start": v(-2.58, 18.54) * mm, "mid": v(-2.61, 18.7) * mm, "end": v(-2.67, 18.85) * mm});
            skArc(sketch, "E42.8.0.2", {"start": v(-2.58, 18.54) * mm, "mid": v(-2.53, 18.44) * mm, "end": v(-2.43, 18.4) * mm});
            skLineSegment(sketch, "E42.8.0.3", {"start": v(-2.43, 18.4) * mm, "end": v(-2.17, 18.4) * mm});
            skArc(sketch, "E42.8.0.4", {"start": v(-3.67, 18.85) * mm, "mid": v(-3.47, 19.07) * mm, "end": v(-3.17, 19.16) * mm});
            skArc(sketch, "E42.8.0.5", {"start": v(-3.76, 18.54) * mm, "mid": v(-3.73, 18.7) * mm, "end": v(-3.67, 18.85) * mm});
            skArc(sketch, "E42.8.0.6", {"start": v(-3.76, 18.54) * mm, "mid": v(-3.81, 18.44) * mm, "end": v(-3.91, 18.4) * mm});
            skLineSegment(sketch, "E42.8.0.7", {"start": v(-3.91, 18.4) * mm, "end": v(-4.17, 18.4) * mm});
            skArc(sketch, "E42.9.0.0", {"start": v(-0.67, 18.85) * mm, "mid": v(-0.88, 19.07) * mm, "end": v(-1.17, 19.16) * mm});
            skArc(sketch, "E42.9.0.1", {"start": v(-0.58, 18.54) * mm, "mid": v(-0.61, 18.7) * mm, "end": v(-0.67, 18.85) * mm});
            skArc(sketch, "E42.9.0.2", {"start": v(-0.58, 18.54) * mm, "mid": v(-0.53, 18.44) * mm, "end": v(-0.43, 18.4) * mm});
            skLineSegment(sketch, "E42.9.0.3", {"start": v(-0.43, 18.4) * mm, "end": v(-0.17, 18.4) * mm});
            skArc(sketch, "E42.9.0.4", {"start": v(-1.67, 18.85) * mm, "mid": v(-1.47, 19.07) * mm, "end": v(-1.17, 19.16) * mm});
            skArc(sketch, "E42.9.0.5", {"start": v(-1.76, 18.54) * mm, "mid": v(-1.73, 18.7) * mm, "end": v(-1.67, 18.85) * mm});
            skArc(sketch, "E42.9.0.6", {"start": v(-1.76, 18.54) * mm, "mid": v(-1.81, 18.44) * mm, "end": v(-1.91, 18.4) * mm});
            skLineSegment(sketch, "E42.9.0.7", {"start": v(-1.91, 18.4) * mm, "end": v(-2.17, 18.4) * mm});
            skArc(sketch, "E42.10.0.0", {"start": v(1.33, 18.85) * mm, "mid": v(1.12, 19.07) * mm, "end": v(0.83, 19.16) * mm});
            skArc(sketch, "E42.10.0.1", {"start": v(1.42, 18.54) * mm, "mid": v(1.39, 18.7) * mm, "end": v(1.33, 18.85) * mm});
            skArc(sketch, "E42.10.0.2", {"start": v(1.42, 18.54) * mm, "mid": v(1.47, 18.44) * mm, "end": v(1.57, 18.4) * mm});
            skLineSegment(sketch, "E42.10.0.3", {"start": v(1.57, 18.4) * mm, "end": v(1.83, 18.4) * mm});
            skArc(sketch, "E42.10.0.4", {"start": v(0.33, 18.85) * mm, "mid": v(0.53, 19.07) * mm, "end": v(0.83, 19.16) * mm});
            skArc(sketch, "E42.10.0.5", {"start": v(0.24, 18.54) * mm, "mid": v(0.27, 18.7) * mm, "end": v(0.33, 18.85) * mm});
            skArc(sketch, "E42.10.0.6", {"start": v(0.24, 18.54) * mm, "mid": v(0.19, 18.44) * mm, "end": v(0.09, 18.4) * mm});
            skLineSegment(sketch, "E42.10.0.7", {"start": v(0.09, 18.4) * mm, "end": v(-0.17, 18.4) * mm});
            skArc(sketch, "E42.11.0.0", {"start": v(3.33, 18.85) * mm, "mid": v(3.12, 19.07) * mm, "end": v(2.83, 19.16) * mm});
            skArc(sketch, "E42.11.0.1", {"start": v(3.42, 18.54) * mm, "mid": v(3.39, 18.7) * mm, "end": v(3.33, 18.85) * mm});
            skArc(sketch, "E42.11.0.2", {"start": v(3.42, 18.54) * mm, "mid": v(3.47, 18.44) * mm, "end": v(3.57, 18.4) * mm});
            skLineSegment(sketch, "E42.11.0.3", {"start": v(3.57, 18.4) * mm, "end": v(3.83, 18.4) * mm});
            skArc(sketch, "E42.11.0.4", {"start": v(2.33, 18.85) * mm, "mid": v(2.53, 19.07) * mm, "end": v(2.83, 19.16) * mm});
            skArc(sketch, "E42.11.0.5", {"start": v(2.24, 18.54) * mm, "mid": v(2.27, 18.7) * mm, "end": v(2.33, 18.85) * mm});
            skArc(sketch, "E42.11.0.6", {"start": v(2.24, 18.54) * mm, "mid": v(2.19, 18.44) * mm, "end": v(2.09, 18.4) * mm});
            skLineSegment(sketch, "E42.11.0.7", {"start": v(2.09, 18.4) * mm, "end": v(1.83, 18.4) * mm});
            skArc(sketch, "E42.12.0.0", {"start": v(5.33, 18.85) * mm, "mid": v(5.12, 19.07) * mm, "end": v(4.83, 19.16) * mm});
            skArc(sketch, "E42.12.0.1", {"start": v(5.42, 18.54) * mm, "mid": v(5.39, 18.7) * mm, "end": v(5.33, 18.85) * mm});
            skArc(sketch, "E42.12.0.2", {"start": v(5.42, 18.54) * mm, "mid": v(5.47, 18.44) * mm, "end": v(5.57, 18.4) * mm});
            skLineSegment(sketch, "E42.12.0.3", {"start": v(5.57, 18.4) * mm, "end": v(5.83, 18.4) * mm});
            skArc(sketch, "E42.12.0.4", {"start": v(4.33, 18.85) * mm, "mid": v(4.53, 19.07) * mm, "end": v(4.83, 19.16) * mm});
            skArc(sketch, "E42.12.0.5", {"start": v(4.24, 18.54) * mm, "mid": v(4.27, 18.7) * mm, "end": v(4.33, 18.85) * mm});
            skArc(sketch, "E42.12.0.6", {"start": v(4.24, 18.54) * mm, "mid": v(4.19, 18.44) * mm, "end": v(4.09, 18.4) * mm});
            skLineSegment(sketch, "E42.12.0.7", {"start": v(4.09, 18.4) * mm, "end": v(3.83, 18.4) * mm});
            skArc(sketch, "E42.13.0.0", {"start": v(7.33, 18.85) * mm, "mid": v(7.12, 19.07) * mm, "end": v(6.83, 19.16) * mm});
            skArc(sketch, "E42.13.0.1", {"start": v(7.42, 18.54) * mm, "mid": v(7.39, 18.7) * mm, "end": v(7.33, 18.85) * mm});
            skArc(sketch, "E42.13.0.2", {"start": v(7.42, 18.54) * mm, "mid": v(7.47, 18.44) * mm, "end": v(7.57, 18.4) * mm});
            skLineSegment(sketch, "E42.13.0.3", {"start": v(7.57, 18.4) * mm, "end": v(7.83, 18.4) * mm});
            skArc(sketch, "E42.13.0.4", {"start": v(6.33, 18.85) * mm, "mid": v(6.53, 19.07) * mm, "end": v(6.83, 19.16) * mm});
            skArc(sketch, "E42.13.0.5", {"start": v(6.24, 18.54) * mm, "mid": v(6.27, 18.7) * mm, "end": v(6.33, 18.85) * mm});
            skArc(sketch, "E42.13.0.6", {"start": v(6.24, 18.54) * mm, "mid": v(6.19, 18.44) * mm, "end": v(6.09, 18.4) * mm});
            skLineSegment(sketch, "E42.13.0.7", {"start": v(6.09, 18.4) * mm, "end": v(5.83, 18.4) * mm});
            skArc(sketch, "E42.14.0.0", {"start": v(9.33, 18.85) * mm, "mid": v(9.12, 19.07) * mm, "end": v(8.83, 19.16) * mm});
            skArc(sketch, "E42.14.0.1", {"start": v(9.42, 18.54) * mm, "mid": v(9.39, 18.7) * mm, "end": v(9.33, 18.85) * mm});
            skArc(sketch, "E42.14.0.2", {"start": v(9.42, 18.54) * mm, "mid": v(9.47, 18.44) * mm, "end": v(9.57, 18.4) * mm});
            skLineSegment(sketch, "E42.14.0.3", {"start": v(9.57, 18.4) * mm, "end": v(9.83, 18.4) * mm});
            skArc(sketch, "E42.14.0.4", {"start": v(8.33, 18.85) * mm, "mid": v(8.53, 19.07) * mm, "end": v(8.83, 19.16) * mm});
            skArc(sketch, "E42.14.0.5", {"start": v(8.24, 18.54) * mm, "mid": v(8.27, 18.7) * mm, "end": v(8.33, 18.85) * mm});
            skArc(sketch, "E42.14.0.6", {"start": v(8.24, 18.54) * mm, "mid": v(8.19, 18.44) * mm, "end": v(8.09, 18.4) * mm});
            skLineSegment(sketch, "E42.14.0.7", {"start": v(8.09, 18.4) * mm, "end": v(7.83, 18.4) * mm});
            skArc(sketch, "E42.15.0.0", {"start": v(11.33, 18.85) * mm, "mid": v(11.12, 19.07) * mm, "end": v(10.83, 19.16) * mm});
            skArc(sketch, "E42.15.0.1", {"start": v(11.42, 18.54) * mm, "mid": v(11.39, 18.7) * mm, "end": v(11.33, 18.85) * mm});
            skArc(sketch, "E42.15.0.2", {"start": v(11.42, 18.54) * mm, "mid": v(11.47, 18.44) * mm, "end": v(11.57, 18.4) * mm});
            skLineSegment(sketch, "E42.15.0.3", {"start": v(11.57, 18.4) * mm, "end": v(11.83, 18.4) * mm});
            skArc(sketch, "E42.15.0.4", {"start": v(10.33, 18.85) * mm, "mid": v(10.53, 19.07) * mm, "end": v(10.83, 19.16) * mm});
            skArc(sketch, "E42.15.0.5", {"start": v(10.24, 18.54) * mm, "mid": v(10.27, 18.7) * mm, "end": v(10.33, 18.85) * mm});
            skArc(sketch, "E42.15.0.6", {"start": v(10.24, 18.54) * mm, "mid": v(10.19, 18.44) * mm, "end": v(10.09, 18.4) * mm});
            skLineSegment(sketch, "E42.15.0.7", {"start": v(10.09, 18.4) * mm, "end": v(9.83, 18.4) * mm});
            skArc(sketch, "E42.16.0.0", {"start": v(13.33, 18.85) * mm, "mid": v(13.12, 19.07) * mm, "end": v(12.83, 19.16) * mm});
            skArc(sketch, "E42.16.0.1", {"start": v(13.42, 18.54) * mm, "mid": v(13.39, 18.7) * mm, "end": v(13.33, 18.85) * mm});
            skArc(sketch, "E42.16.0.2", {"start": v(13.42, 18.54) * mm, "mid": v(13.47, 18.44) * mm, "end": v(13.57, 18.4) * mm});
            skLineSegment(sketch, "E42.16.0.3", {"start": v(13.57, 18.4) * mm, "end": v(13.83, 18.4) * mm});
            skArc(sketch, "E42.16.0.4", {"start": v(12.33, 18.85) * mm, "mid": v(12.53, 19.07) * mm, "end": v(12.83, 19.16) * mm});
            skArc(sketch, "E42.16.0.5", {"start": v(12.24, 18.54) * mm, "mid": v(12.27, 18.7) * mm, "end": v(12.33, 18.85) * mm});
            skArc(sketch, "E42.16.0.6", {"start": v(12.24, 18.54) * mm, "mid": v(12.19, 18.44) * mm, "end": v(12.09, 18.4) * mm});
            skLineSegment(sketch, "E42.16.0.7", {"start": v(12.09, 18.4) * mm, "end": v(11.83, 18.4) * mm});
            skArc(sketch, "E42.17.0.0", {"start": v(15.33, 18.85) * mm, "mid": v(15.12, 19.07) * mm, "end": v(14.83, 19.16) * mm});
            skArc(sketch, "E42.17.0.1", {"start": v(15.42, 18.54) * mm, "mid": v(15.39, 18.7) * mm, "end": v(15.33, 18.85) * mm});
            skArc(sketch, "E42.17.0.2", {"start": v(15.42, 18.54) * mm, "mid": v(15.47, 18.44) * mm, "end": v(15.57, 18.4) * mm});
            skLineSegment(sketch, "E42.17.0.3", {"start": v(15.57, 18.4) * mm, "end": v(15.83, 18.4) * mm});
            skArc(sketch, "E42.17.0.4", {"start": v(14.33, 18.85) * mm, "mid": v(14.53, 19.07) * mm, "end": v(14.83, 19.16) * mm});
            skArc(sketch, "E42.17.0.5", {"start": v(14.24, 18.54) * mm, "mid": v(14.27, 18.7) * mm, "end": v(14.33, 18.85) * mm});
            skArc(sketch, "E42.17.0.6", {"start": v(14.24, 18.54) * mm, "mid": v(14.19, 18.44) * mm, "end": v(14.09, 18.4) * mm});
            skLineSegment(sketch, "E42.17.0.7", {"start": v(14.09, 18.4) * mm, "end": v(13.83, 18.4) * mm});
            skArc(sketch, "E42.18.0.0", {"start": v(17.33, 18.85) * mm, "mid": v(17.12, 19.07) * mm, "end": v(16.83, 19.16) * mm});
            skArc(sketch, "E42.18.0.1", {"start": v(17.42, 18.54) * mm, "mid": v(17.39, 18.7) * mm, "end": v(17.33, 18.85) * mm});
            skArc(sketch, "E42.18.0.2", {"start": v(17.42, 18.54) * mm, "mid": v(17.47, 18.44) * mm, "end": v(17.57, 18.4) * mm});
            skLineSegment(sketch, "E42.18.0.3", {"start": v(17.57, 18.4) * mm, "end": v(17.83, 18.4) * mm});
            skArc(sketch, "E42.18.0.4", {"start": v(16.33, 18.85) * mm, "mid": v(16.53, 19.07) * mm, "end": v(16.83, 19.16) * mm});
            skArc(sketch, "E42.18.0.5", {"start": v(16.24, 18.54) * mm, "mid": v(16.27, 18.7) * mm, "end": v(16.33, 18.85) * mm});
            skArc(sketch, "E42.18.0.6", {"start": v(16.24, 18.54) * mm, "mid": v(16.19, 18.44) * mm, "end": v(16.09, 18.4) * mm});
            skLineSegment(sketch, "E42.18.0.7", {"start": v(16.09, 18.4) * mm, "end": v(15.83, 18.4) * mm});
            skArc(sketch, "E42.19.0.0", {"start": v(19.33, 18.85) * mm, "mid": v(19.12, 19.07) * mm, "end": v(18.83, 19.16) * mm});
            skArc(sketch, "E42.19.0.1", {"start": v(19.42, 18.54) * mm, "mid": v(19.39, 18.7) * mm, "end": v(19.33, 18.85) * mm});
            skArc(sketch, "E42.19.0.2", {"start": v(19.42, 18.54) * mm, "mid": v(19.47, 18.44) * mm, "end": v(19.57, 18.4) * mm});
            skLineSegment(sketch, "E42.19.0.3", {"start": v(19.57, 18.4) * mm, "end": v(19.83, 18.4) * mm});
            skArc(sketch, "E42.19.0.4", {"start": v(18.33, 18.85) * mm, "mid": v(18.53, 19.07) * mm, "end": v(18.83, 19.16) * mm});
            skArc(sketch, "E42.19.0.5", {"start": v(18.24, 18.54) * mm, "mid": v(18.27, 18.7) * mm, "end": v(18.33, 18.85) * mm});
            skArc(sketch, "E42.19.0.6", {"start": v(18.24, 18.54) * mm, "mid": v(18.19, 18.44) * mm, "end": v(18.09, 18.4) * mm});
            skLineSegment(sketch, "E42.19.0.7", {"start": v(18.09, 18.4) * mm, "end": v(17.83, 18.4) * mm});
            skLineSegment(sketch, "E42.direction1", {"start": v(-20.17, 18.4) * mm, "end": v(-18.17, 18.4) * mm, "construction": true});
            skLineSegment(sketch, "E43", {"start": v(19.83, 18.4) * mm, "end": v(19.83, 17.78) * mm});
            skLineSegment(sketch, "E44", {"start": v(19.83, 17.78) * mm, "end": v(-18.17, 17.78) * mm});
            skSolve(sketch);
        }
        {
            var Q0;
            Q0=makeQuery(id+"F0.imprint","IMPRINT",FACE,{"disambiguationData":[TD([[makeQuery(id+"F0.imprint","IMPRINT",EDGE,{"derivedFrom":sQuery(id+"F0.wireOp",EDGE,"E15")}),-1.0]])]});
            extrude(context, id + "F1", {"entities" : qUnion([Q0]), "depth" : 7.5 * mm});
        }
        {
            var Q0;
            Q0=makeQuery(id+"F1.opExtrude","CAP_FACE",FACE,{"disambiguationData":[OSD([sQuery(id+"F0.wireOp",EDGE,"E15"),sQuery(id+"F0.wireOp",EDGE,"E16"),sQuery(id+"F0.wireOp",EDGE,"E17"),sQuery(id+"F0.wireOp",EDGE,"E18"),sQuery(id+"F0.wireOp",EDGE,"E19"),sQuery(id+"F0.wireOp",EDGE,"E20"),sQuery(id+"F0.wireOp",EDGE,"E21.1.0"),sQuery(id+"F0.wireOp",EDGE,"E21.1.2"),sQuery(id+"F0.wireOp",EDGE,"E21.1.3"),sQuery(id+"F0.wireOp",EDGE,"E21.1.4"),sQuery(id+"F0.wireOp",EDGE,"E21.1.5"),sQuery(id+"F0.wireOp",EDGE,"E22.3.2.0"),sQuery(id+"F0.wireOp",EDGE,"E22.5.2.0"),sQuery(id+"F0.wireOp",EDGE,"E22.9.2.0"),sQuery(id+"F0.wireOp",EDGE,"E22.13.2.0"),sQuery(id+"F0.wireOp",EDGE,"E22.17.2.0"),sQuery(id+"F0.wireOp",EDGE,"E22.3.3.0"),sQuery(id+"F0.wireOp",EDGE,"E22.5.3.0"),sQuery(id+"F0.wireOp",EDGE,"E22.9.3.0"),sQuery(id+"F0.wireOp",EDGE,"E22.13.3.0"),sQuery(id+"F0.wireOp",EDGE,"E22.17.3.0"),sQuery(id+"F0.wireOp",EDGE,"E22.3.4.0"),sQuery(id+"F0.wireOp",EDGE,"E22.5.4.0"),sQuery(id+"F0.wireOp",EDGE,"E22.9.4.0"),sQuery(id+"F0.wireOp",EDGE,"E22.13.4.0"),sQuery(id+"F0.wireOp",EDGE,"E22.17.4.0"),sQuery(id+"F0.wireOp",EDGE,"E22.3.5.0"),sQuery(id+"F0.wireOp",EDGE,"E22.5.5.0"),sQuery(id+"F0.wireOp",EDGE,"E22.9.5.0"),sQuery(id+"F0.wireOp",EDGE,"E22.13.5.0"),sQuery(id+"F0.wireOp",EDGE,"E22.17.5.0"),sQuery(id+"F0.wireOp",EDGE,"E22.3.6.0"),sQuery(id+"F0.wireOp",EDGE,"E22.5.6.0"),sQuery(id+"F0.wireOp",EDGE,"E22.9.6.0"),sQuery(id+"F0.wireOp",EDGE,"E22.13.6.0"),sQuery(id+"F0.wireOp",EDGE,"E22.17.6.0"),sQuery(id+"F0.wireOp",EDGE,"E22.3.7.0"),sQuery(id+"F0.wireOp",EDGE,"E22.5.7.0"),sQuery(id+"F0.wireOp",EDGE,"E22.9.7.0"),sQuery(id+"F0.wireOp",EDGE,"E22.13.7.0"),sQuery(id+"F0.wireOp",EDGE,"E22.17.7.0"),sQuery(id+"F0.wireOp",EDGE,"E22.3.8.0"),sQuery(id+"F0.wireOp",EDGE,"E22.5.8.0"),sQuery(id+"F0.wireOp",EDGE,"E22.9.8.0"),sQuery(id+"F0.wireOp",EDGE,"E22.13.8.0"),sQuery(id+"F0.wireOp",EDGE,"E22.17.8.0"),sQuery(id+"F0.wireOp",EDGE,"E22.3.9.0"),sQuery(id+"F0.wireOp",EDGE,"E22.5.9.0"),sQuery(id+"F0.wireOp",EDGE,"E22.9.9.0"),sQuery(id+"F0.wireOp",EDGE,"E22.13.9.0"),sQuery(id+"F0.wireOp",EDGE,"E22.17.9.0"),sQuery(id+"F0.wireOp",EDGE,"E22.3.10.0"),sQuery(id+"F0.wireOp",EDGE,"E22.5.10.0"),sQuery(id+"F0.wireOp",EDGE,"E22.9.10.0"),sQuery(id+"F0.wireOp",EDGE,"E22.13.10.0"),sQuery(id+"F0.wireOp",EDGE,"E22.17.10.0"),sQuery(id+"F0.wireOp",EDGE,"E22.3.11.0"),sQuery(id+"F0.wireOp",EDGE,"E22.5.11.0"),sQuery(id+"F0.wireOp",EDGE,"E22.9.11.0"),sQuery(id+"F0.wireOp",EDGE,"E22.13.11.0"),sQuery(id+"F0.wireOp",EDGE,"E22.17.11.0"),sQuery(id+"F0.wireOp",EDGE,"E22.3.12.0"),sQuery(id+"F0.wireOp",EDGE,"E22.5.12.0"),sQuery(id+"F0.wireOp",EDGE,"E22.9.12.0"),sQuery(id+"F0.wireOp",EDGE,"E22.13.12.0"),sQuery(id+"F0.wireOp",EDGE,"E22.17.12.0"),sQuery(id+"F0.wireOp",EDGE,"E22.3.13.0"),sQuery(id+"F0.wireOp",EDGE,"E22.5.13.0"),sQuery(id+"F0.wireOp",EDGE,"E22.9.13.0"),sQuery(id+"F0.wireOp",EDGE,"E22.13.13.0"),sQuery(id+"F0.wireOp",EDGE,"E22.17.13.0"),sQuery(id+"F0.wireOp",EDGE,"E22.3.14.0"),sQuery(id+"F0.wireOp",EDGE,"E22.5.14.0"),sQuery(id+"F0.wireOp",EDGE,"E22.9.14.0"),sQuery(id+"F0.wireOp",EDGE,"E22.13.14.0"),sQuery(id+"F0.wireOp",EDGE,"E22.17.14.0"),sQuery(id+"F0.wireOp",EDGE,"E22.3.15.0"),sQuery(id+"F0.wireOp",EDGE,"E22.5.15.0"),sQuery(id+"F0.wireOp",EDGE,"E22.9.15.0"),sQuery(id+"F0.wireOp",EDGE,"E22.13.15.0"),sQuery(id+"F0.wireOp",EDGE,"E22.17.15.0"),sQuery(id+"F0.wireOp",EDGE,"E22.3.16.0"),sQuery(id+"F0.wireOp",EDGE,"E22.5.16.0"),sQuery(id+"F0.wireOp",EDGE,"E22.9.16.0"),sQuery(id+"F0.wireOp",EDGE,"E22.13.16.0"),sQuery(id+"F0.wireOp",EDGE,"E22.17.16.0"),sQuery(id+"F0.wireOp",EDGE,"E22.3.17.0"),sQuery(id+"F0.wireOp",EDGE,"E22.5.17.0"),sQuery(id+"F0.wireOp",EDGE,"E22.9.17.0"),sQuery(id+"F0.wireOp",EDGE,"E22.13.17.0"),sQuery(id+"F0.wireOp",EDGE,"E22.17.17.0"),sQuery(id+"F0.wireOp",EDGE,"E22.3.18.0"),sQuery(id+"F0.wireOp",EDGE,"E22.5.18.0"),sQuery(id+"F0.wireOp",EDGE,"E22.9.18.0"),sQuery(id+"F0.wireOp",EDGE,"E22.13.18.0"),sQuery(id+"F0.wireOp",EDGE,"E22.17.18.0"),sQuery(id+"F0.wireOp",EDGE,"E22.3.19.0"),sQuery(id+"F0.wireOp",EDGE,"E22.5.19.0"),sQuery(id+"F0.wireOp",EDGE,"E22.9.19.0"),sQuery(id+"F0.wireOp",EDGE,"E22.13.19.0"),sQuery(id+"F0.wireOp",EDGE,"E22.17.19.0"),sQuery(id+"F0.wireOp",EDGE,"E23.trimOffspring"),sQuery(id+"F0.wireOp",EDGE,"E24.trimOffspring"),sQuery(id+"F0.wireOp",EDGE,"E25.trimOffspring"),sQuery(id+"F0.wireOp",EDGE,"E26.trimOffspring"),sQuery(id+"F0.wireOp",EDGE,"E27.trimOffspring"),sQuery(id+"F0.wireOp",EDGE,"E28.trimOffspring"),sQuery(id+"F0.wireOp",EDGE,"E29.trimOffspring"),sQuery(id+"F0.wireOp",EDGE,"E30.trimOffspring"),sQuery(id+"F0.wireOp",EDGE,"E31.trimOffspring"),sQuery(id+"F0.wireOp",EDGE,"E32.trimOffspring"),sQuery(id+"F0.wireOp",EDGE,"E33.trimOffspring"),sQuery(id+"F0.wireOp",EDGE,"E34.trimOffspring"),sQuery(id+"F0.wireOp",EDGE,"E35.trimOffspring"),sQuery(id+"F0.wireOp",EDGE,"E36.trimOffspring"),sQuery(id+"F0.wireOp",EDGE,"E37.trimOffspring"),sQuery(id+"F0.wireOp",EDGE,"E38.trimOffspring"),sQuery(id+"F0.wireOp",EDGE,"E39.trimOffspring"),sQuery(id+"F0.wireOp",EDGE,"E40.trimOffspring"),sQuery(id+"F0.wireOp",EDGE,"E41.trimOffspring")])],"isStart":false});
            var sketch = newSketch(context, id + "F2", { "sketchPlane" : qUnion([Q0])});
            skCircle(sketch, "E45", {"center": v(0, 0) * mm, "radius": 8 * mm});
            skSolve(sketch);
        }
        {
            var Q0;
            Q0=qSketchRegion(id+"F2",true);
            extrude(context, id + "F3", {"entities" : qUnion([Q0]), "operationType" : NewBodyOperationType.ADD, "depth" : 9 * mm});
        }
        {
            var Q0;
            Q0=makeQuery(id+"F1.opExtrude","CAP_FACE",FACE,{"disambiguationData":[OSD([sQuery(id+"F0.wireOp",EDGE,"E15"),sQuery(id+"F0.wireOp",EDGE,"E16"),sQuery(id+"F0.wireOp",EDGE,"E17"),sQuery(id+"F0.wireOp",EDGE,"E18"),sQuery(id+"F0.wireOp",EDGE,"E19"),sQuery(id+"F0.wireOp",EDGE,"E20"),sQuery(id+"F0.wireOp",EDGE,"E21.1.0"),sQuery(id+"F0.wireOp",EDGE,"E21.1.2"),sQuery(id+"F0.wireOp",EDGE,"E21.1.3"),sQuery(id+"F0.wireOp",EDGE,"E21.1.4"),sQuery(id+"F0.wireOp",EDGE,"E21.1.5"),sQuery(id+"F0.wireOp",EDGE,"E22.3.2.0"),sQuery(id+"F0.wireOp",EDGE,"E22.5.2.0"),sQuery(id+"F0.wireOp",EDGE,"E22.9.2.0"),sQuery(id+"F0.wireOp",EDGE,"E22.13.2.0"),sQuery(id+"F0.wireOp",EDGE,"E22.17.2.0"),sQuery(id+"F0.wireOp",EDGE,"E22.3.3.0"),sQuery(id+"F0.wireOp",EDGE,"E22.5.3.0"),sQuery(id+"F0.wireOp",EDGE,"E22.9.3.0"),sQuery(id+"F0.wireOp",EDGE,"E22.13.3.0"),sQuery(id+"F0.wireOp",EDGE,"E22.17.3.0"),sQuery(id+"F0.wireOp",EDGE,"E22.3.4.0"),sQuery(id+"F0.wireOp",EDGE,"E22.5.4.0"),sQuery(id+"F0.wireOp",EDGE,"E22.9.4.0"),sQuery(id+"F0.wireOp",EDGE,"E22.13.4.0"),sQuery(id+"F0.wireOp",EDGE,"E22.17.4.0"),sQuery(id+"F0.wireOp",EDGE,"E22.3.5.0"),sQuery(id+"F0.wireOp",EDGE,"E22.5.5.0"),sQuery(id+"F0.wireOp",EDGE,"E22.9.5.0"),sQuery(id+"F0.wireOp",EDGE,"E22.13.5.0"),sQuery(id+"F0.wireOp",EDGE,"E22.17.5.0"),sQuery(id+"F0.wireOp",EDGE,"E22.3.6.0"),sQuery(id+"F0.wireOp",EDGE,"E22.5.6.0"),sQuery(id+"F0.wireOp",EDGE,"E22.9.6.0"),sQuery(id+"F0.wireOp",EDGE,"E22.13.6.0"),sQuery(id+"F0.wireOp",EDGE,"E22.17.6.0"),sQuery(id+"F0.wireOp",EDGE,"E22.3.7.0"),sQuery(id+"F0.wireOp",EDGE,"E22.5.7.0"),sQuery(id+"F0.wireOp",EDGE,"E22.9.7.0"),sQuery(id+"F0.wireOp",EDGE,"E22.13.7.0"),sQuery(id+"F0.wireOp",EDGE,"E22.17.7.0"),sQuery(id+"F0.wireOp",EDGE,"E22.3.8.0"),sQuery(id+"F0.wireOp",EDGE,"E22.5.8.0"),sQuery(id+"F0.wireOp",EDGE,"E22.9.8.0"),sQuery(id+"F0.wireOp",EDGE,"E22.13.8.0"),sQuery(id+"F0.wireOp",EDGE,"E22.17.8.0"),sQuery(id+"F0.wireOp",EDGE,"E22.3.9.0"),sQuery(id+"F0.wireOp",EDGE,"E22.5.9.0"),sQuery(id+"F0.wireOp",EDGE,"E22.9.9.0"),sQuery(id+"F0.wireOp",EDGE,"E22.13.9.0"),sQuery(id+"F0.wireOp",EDGE,"E22.17.9.0"),sQuery(id+"F0.wireOp",EDGE,"E22.3.10.0"),sQuery(id+"F0.wireOp",EDGE,"E22.5.10.0"),sQuery(id+"F0.wireOp",EDGE,"E22.9.10.0"),sQuery(id+"F0.wireOp",EDGE,"E22.13.10.0"),sQuery(id+"F0.wireOp",EDGE,"E22.17.10.0"),sQuery(id+"F0.wireOp",EDGE,"E22.3.11.0"),sQuery(id+"F0.wireOp",EDGE,"E22.5.11.0"),sQuery(id+"F0.wireOp",EDGE,"E22.9.11.0"),sQuery(id+"F0.wireOp",EDGE,"E22.13.11.0"),sQuery(id+"F0.wireOp",EDGE,"E22.17.11.0"),sQuery(id+"F0.wireOp",EDGE,"E22.3.12.0"),sQuery(id+"F0.wireOp",EDGE,"E22.5.12.0"),sQuery(id+"F0.wireOp",EDGE,"E22.9.12.0"),sQuery(id+"F0.wireOp",EDGE,"E22.13.12.0"),sQuery(id+"F0.wireOp",EDGE,"E22.17.12.0"),sQuery(id+"F0.wireOp",EDGE,"E22.3.13.0"),sQuery(id+"F0.wireOp",EDGE,"E22.5.13.0"),sQuery(id+"F0.wireOp",EDGE,"E22.9.13.0"),sQuery(id+"F0.wireOp",EDGE,"E22.13.13.0"),sQuery(id+"F0.wireOp",EDGE,"E22.17.13.0"),sQuery(id+"F0.wireOp",EDGE,"E22.3.14.0"),sQuery(id+"F0.wireOp",EDGE,"E22.5.14.0"),sQuery(id+"F0.wireOp",EDGE,"E22.9.14.0"),sQuery(id+"F0.wireOp",EDGE,"E22.13.14.0"),sQuery(id+"F0.wireOp",EDGE,"E22.17.14.0"),sQuery(id+"F0.wireOp",EDGE,"E22.3.15.0"),sQuery(id+"F0.wireOp",EDGE,"E22.5.15.0"),sQuery(id+"F0.wireOp",EDGE,"E22.9.15.0"),sQuery(id+"F0.wireOp",EDGE,"E22.13.15.0"),sQuery(id+"F0.wireOp",EDGE,"E22.17.15.0"),sQuery(id+"F0.wireOp",EDGE,"E22.3.16.0"),sQuery(id+"F0.wireOp",EDGE,"E22.5.16.0"),sQuery(id+"F0.wireOp",EDGE,"E22.9.16.0"),sQuery(id+"F0.wireOp",EDGE,"E22.13.16.0"),sQuery(id+"F0.wireOp",EDGE,"E22.17.16.0"),sQuery(id+"F0.wireOp",EDGE,"E22.3.17.0"),sQuery(id+"F0.wireOp",EDGE,"E22.5.17.0"),sQuery(id+"F0.wireOp",EDGE,"E22.9.17.0"),sQuery(id+"F0.wireOp",EDGE,"E22.13.17.0"),sQuery(id+"F0.wireOp",EDGE,"E22.17.17.0"),sQuery(id+"F0.wireOp",EDGE,"E22.3.18.0"),sQuery(id+"F0.wireOp",EDGE,"E22.5.18.0"),sQuery(id+"F0.wireOp",EDGE,"E22.9.18.0"),sQuery(id+"F0.wireOp",EDGE,"E22.13.18.0"),sQuery(id+"F0.wireOp",EDGE,"E22.17.18.0"),sQuery(id+"F0.wireOp",EDGE,"E22.3.19.0"),sQuery(id+"F0.wireOp",EDGE,"E22.5.19.0"),sQuery(id+"F0.wireOp",EDGE,"E22.9.19.0"),sQuery(id+"F0.wireOp",EDGE,"E22.13.19.0"),sQuery(id+"F0.wireOp",EDGE,"E22.17.19.0"),sQuery(id+"F0.wireOp",EDGE,"E23.trimOffspring"),sQuery(id+"F0.wireOp",EDGE,"E24.trimOffspring"),sQuery(id+"F0.wireOp",EDGE,"E25.trimOffspring"),sQuery(id+"F0.wireOp",EDGE,"E26.trimOffspring"),sQuery(id+"F0.wireOp",EDGE,"E27.trimOffspring"),sQuery(id+"F0.wireOp",EDGE,"E28.trimOffspring"),sQuery(id+"F0.wireOp",EDGE,"E29.trimOffspring"),sQuery(id+"F0.wireOp",EDGE,"E30.trimOffspring"),sQuery(id+"F0.wireOp",EDGE,"E31.trimOffspring"),sQuery(id+"F0.wireOp",EDGE,"E32.trimOffspring"),sQuery(id+"F0.wireOp",EDGE,"E33.trimOffspring"),sQuery(id+"F0.wireOp",EDGE,"E34.trimOffspring"),sQuery(id+"F0.wireOp",EDGE,"E35.trimOffspring"),sQuery(id+"F0.wireOp",EDGE,"E36.trimOffspring"),sQuery(id+"F0.wireOp",EDGE,"E37.trimOffspring"),sQuery(id+"F0.wireOp",EDGE,"E38.trimOffspring"),sQuery(id+"F0.wireOp",EDGE,"E39.trimOffspring"),sQuery(id+"F0.wireOp",EDGE,"E40.trimOffspring"),sQuery(id+"F0.wireOp",EDGE,"E41.trimOffspring")])],"isStart":true});
            var sketch = newSketch(context, id + "F4", { "sketchPlane" : qUnion([Q0])});
            skCircle(sketch, "E46", {"center": v(0, 0) * mm, "radius": 8 * mm});
            skSolve(sketch);
        }
        {
            var Q0;
            Q0=qSketchRegion(id+"F4",true);
            extrude(context, id + "F5", {"entities" : qUnion([Q0]), "operationType" : NewBodyOperationType.ADD, "depth" : 1.5 * mm});
        }
        {
            var Q0;
            Q0=makeQuery(id+"F5.opExtrude","CAP_FACE",FACE,{"disambiguationData":[OSD([sQuery(id+"F4.wireOp",EDGE,"E46")])],"isStart":false});
            var sketch = newSketch(context, id + "F6", { "sketchPlane" : qUnion([Q0])});
            skCircle(sketch, "E47", {"center": v(0, 0) * mm, "radius": 2.5 * mm});
            skSolve(sketch);
        }
        {
            var Q0;
            Q0=qSketchRegion(id+"F6",true);
            extrude(context, id + "F7", {"entities" : qUnion([Q0]), "operationType" : NewBodyOperationType.REMOVE, "endBound" : BoundingType.THROUGH_ALL, "oppositeDirection" : true, "depth" : 25 * mm});
        }
        {
            var Q0;
            Q0=qCreatedBy(makeId("Right.planeOp"),FACE);
            var sketch = newSketch(context, id + "F8", { "sketchPlane" : qUnion([Q0])});
            skCircle(sketch, "E48", {"center": v(0, 12) * mm, "radius": 1.5 * mm});
            skSolve(sketch);
        }
        {
            var Q0;
            Q0=qSketchRegion(id+"F8",true);
            extrude(context, id + "F9", {"entities" : qUnion([Q0]), "operationType" : NewBodyOperationType.REMOVE, "endBound" : BoundingType.THROUGH_ALL, "oppositeDirection" : true, "depth" : 25 * mm});
        }
        {
            var Q0;
            Q0=qCreatedBy(makeId("Front.planeOp"),FACE);
            var sketch = newSketch(context, id + "F10", { "sketchPlane" : qUnion([Q0])});
            skCircle(sketch, "E49", {"center": v(0, 12) * mm, "radius": 1.5 * mm});
            skSolve(sketch);
        }
        {
            var Q0;
            Q0=qSketchRegion(id+"F10",true);
            extrude(context, id + "F11", {"entities" : qUnion([Q0]), "operationType" : NewBodyOperationType.REMOVE, "endBound" : BoundingType.THROUGH_ALL, "oppositeDirection" : true, "depth" : 25 * mm});
        }
        {
            var Q0;
            Q0=makeQuery(id+"F0.imprint","IMPRINT",FACE,{"disambiguationData":[TD([[makeQuery(id+"F0.imprint","IMPRINT",EDGE,{"derivedFrom":sQuery(id+"F0.wireOp",EDGE,"E1")}),-1.0]])]});
            extrude(context, id + "F12", {"entities" : qUnion([Q0]), "depth" : 6 * mm});
        }
    });
